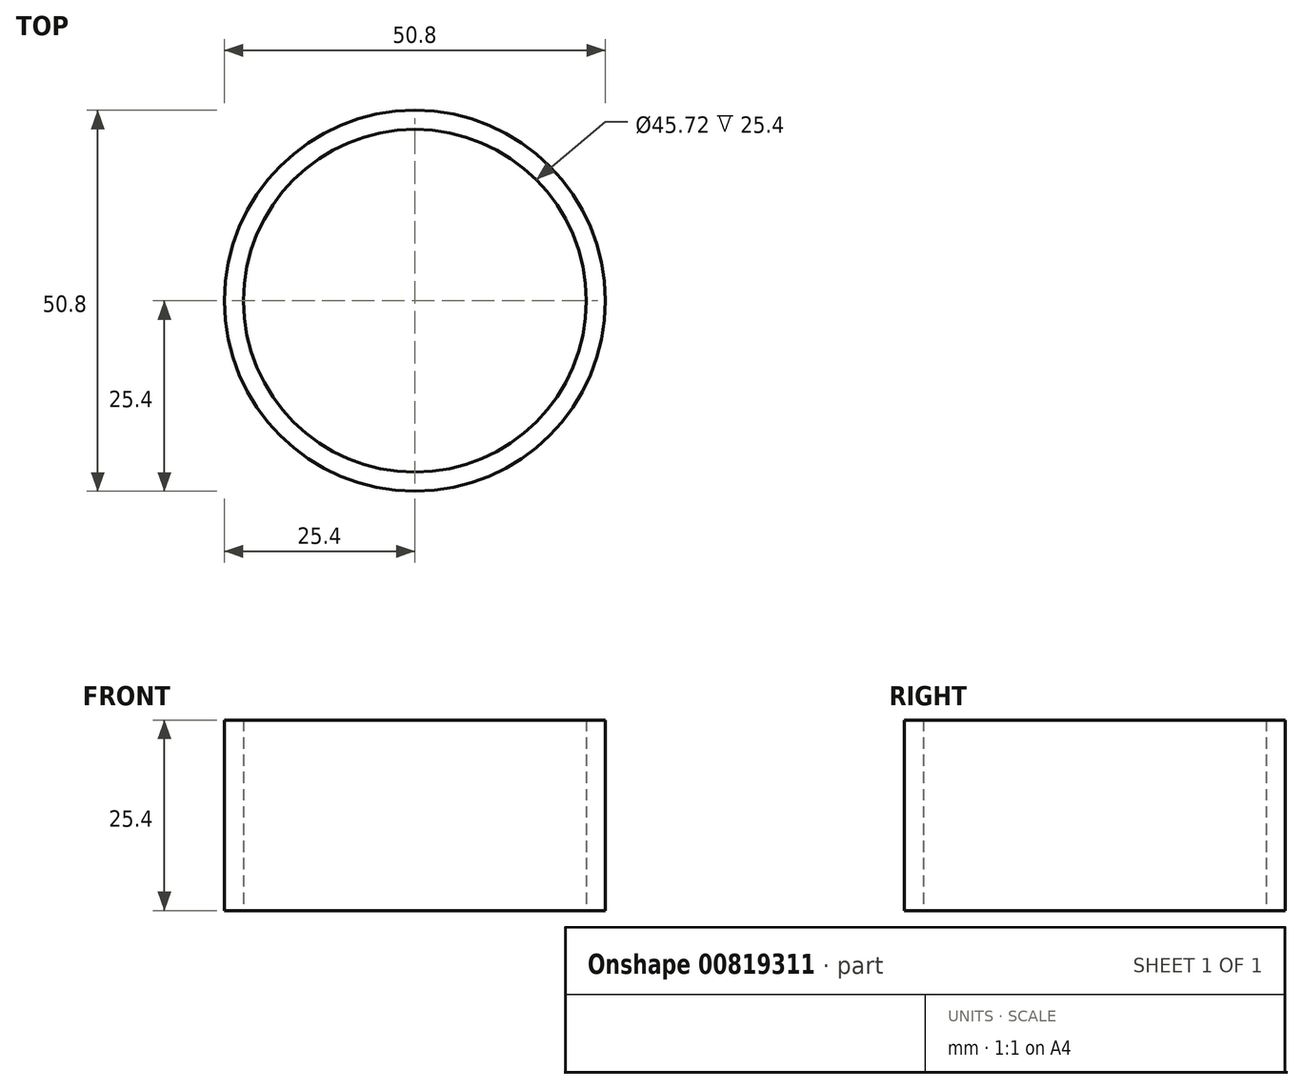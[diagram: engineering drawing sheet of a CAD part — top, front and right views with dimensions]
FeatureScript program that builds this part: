
annotation { "Feature Type Name" : "Feature", "Feature Type Description" : "" }
export const myFeature = defineFeature(function(context is Context, id is Id, definition is map)
    precondition{}
    {
        {
            var Q0;
            Q0=qCreatedBy(makeId("Top.planeOp"),FACE);
            var sketch = newSketch(context, id + "F0", { "sketchPlane" : qUnion([Q0])});
            skCircle(sketch, "E0", {"center": v(0, 0) * mm, "radius": 25.4 * mm});
            skCircle(sketch, "E1.0", {"center": v(0, 0) * mm, "radius": 22.86 * mm});
            skSolve(sketch);
        }
        {
            var Q0;
            Q0 = qSketchRegion(id + "F0", true);
            extrude(context, id + "F1", {"entities" : qUnion([Q0]), "depth" : 25.4 * mm, "offsetDistance" : 25.4 * mm});
        }
    });
